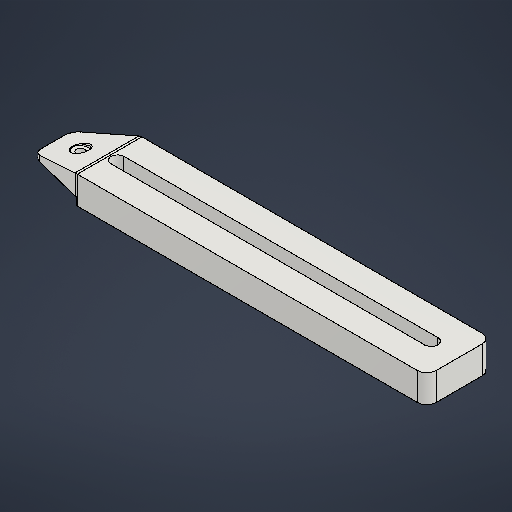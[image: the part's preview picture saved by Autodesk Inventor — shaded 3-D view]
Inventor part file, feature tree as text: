
AUTODESK INVENTOR PART (.ipt)
format: ipt  version: 2025.3 (Build 293356000, 356)  size: 275,968 bytes
history: native  units: mm
features: sketch x4, extrude x3, fillet x2, projected_geometry x2, hole x1, chamfer x1
ambient origin geometry x8: Origin, YZ Plane, XZ Plane, XY Plane, X Axis, Y Axis, Z Axis, Center Point
bodies: Solid1 (feature_tree)
feature tree (13):
  extrude  "Extrusion1"  Depth=35.0mm
  extrude  "Extrusion2"  Depth=170.0mm
  extrude  "Extrusion4"  Depth=20.0mm
  fillet  "Fillet2"  Radius=15.0mm
  fillet  "Fillet1"  [1 undecoded]
  hole  "Hole1"  [1 undecoded]
  chamfer  "Chamfer1"  Distance=5.0mm
  sketch  "Sketch1"  dims[d0=220.0mm d1=35.0mm]
  sketch  "Sketch2"  dims[d2=7.0mm d3=170.0mm]
  sketch  "Sketch3"  dims[d4=15.0mm d6=20.0mm d7=15.0mm d8=0.0mm d12=0.0mm d13=0.0mm]
  projected_geometry  "Projected Loop1"
  sketch  "Sketch5"  dims[d14=0.0mm d15=6.0mm d16=5.0mm d17=4.0mm d18=30.0mm d19=4.5mm d20=6.0mm d21=8.0mm d22=6.0mm d23=90.0deg d24=8.0mm d25=20.594885mm d26=0.5mm d27=2.0mm d28=45.0deg d31=6.0mm d32=170.0mm d33=10.0mm d34=0.0mm d35=3.5mm]
  projected_geometry  "Projected Loop3"
note: 2 required parameter values undecoded (feature->parameter linkage not recoverable at this tier; creation-order binding heuristic only, values carry confidence <= 0.55)
